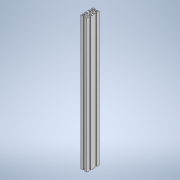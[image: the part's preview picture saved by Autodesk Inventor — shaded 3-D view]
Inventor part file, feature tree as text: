
AUTODESK INVENTOR PART (.ipt)
format: ipt  version: 2022 (Build 260153000, 153)  size: 195,584 bytes
history: native  units: in
note: dims shown in document units (in); Inventor stores cm internally (conversion verified against a paired STEP export)
features: sketch x3, plane x1, extrude x1, hole x1
ambient origin geometry x8: Origin, YZ Plane, XZ Plane, XY Plane, X Axis, Y Axis, Z Axis, Center Point
bodies: Body1 (feature_tree)
feature tree (6):
  plane  "Work Plane1"
  extrude  "Extrusion1"  Depth=16.9685in TaperAngle=0.0deg
  hole  "Hole1"  [1 undecoded]
  sketch  "Sketch1"  dims[d0=16.9685in d1=16.9685in d2=0.0in]
  sketch  "Sketch2"  dims[d3=0.1575in d4=0.2362in d5=0.1575in d6=0.0787in d7=90.0deg d8=0.315in d9=0.8108in]
  sketch  "Sketch3"  dims[d10=0.1575in d11=0.2362in d12=0.1575in d13=0.0787in d14=90.0deg d15=0.315in d16=0.8108in]
note: 1 required parameter value undecoded (feature->parameter linkage not recoverable at this tier; creation-order binding heuristic only, values carry confidence <= 0.55)
